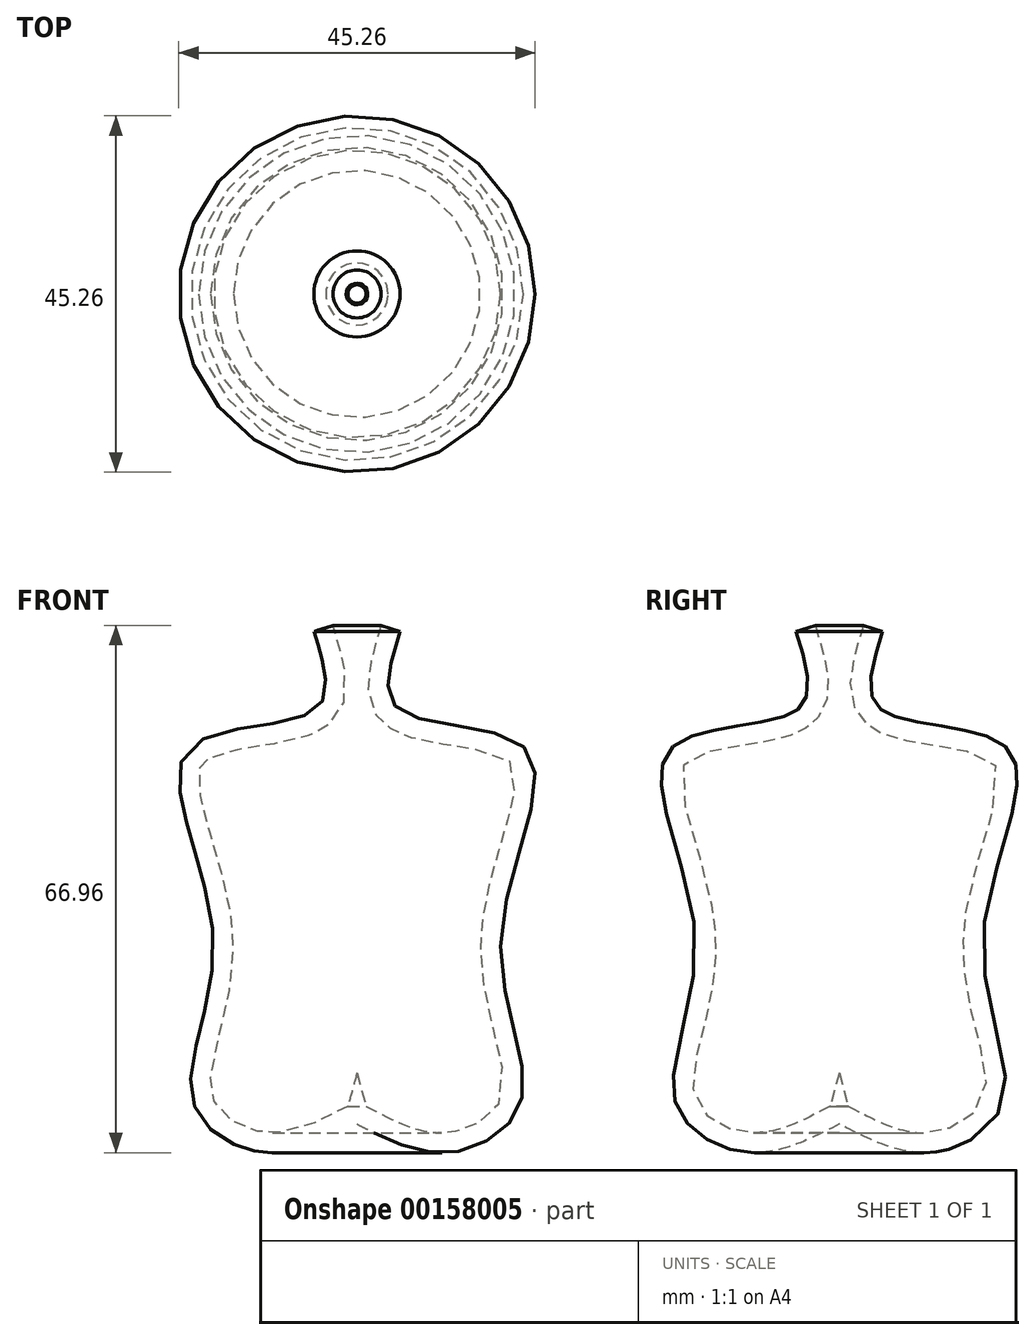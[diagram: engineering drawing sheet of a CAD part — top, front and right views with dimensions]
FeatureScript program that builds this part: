
annotation { "Feature Type Name" : "Feature", "Feature Type Description" : "" }
export const myFeature = defineFeature(function(context is Context, id is Id, definition is map)
    precondition{}
    {
        {
            var Q0;
            Q0=qCreatedBy(makeId("Front.planeOp"),FACE);
            var sketch = newSketch(context, id + "F0", { "sketchPlane" : qUnion([Q0])});
            skFitSpline(sketch, "E0", {"points": [v(0, 0) * mm, v(11.8, -3.6) * mm, v(20.86, 2.9) * mm, v(18.3, 23.93) * mm, v(21.54, 47.53) * mm, v(5.3, 52.66) * mm, v(4.44, 58.98) * mm, v(5.47, 62.57) * mm], "startDerivative": vector(81.88, -42.1) * mm, "endDerivative": vector(12.45, 40.09) * mm});
            skFitSpline(sketch, "E1.0", {"points": [v(1.16, 2.26) * mm, v(2.01, 1.82) * mm, v(3.68, 0.96) * mm, v(6.08, -0.12) * mm, v(7.98, -0.73) * mm, v(9.44, -1.01) * mm, v(10.32, -1.1) * mm, v(11.03, -1.1) * mm, v(11.55, -1.07) * mm, v(12.08, -1) * mm, v(12.8, -0.88) * mm, v(13.7, -0.63) * mm, v(14.75, -0.22) * mm, v(15.72, 0.31) * mm, v(16.59, 0.93) * mm, v(17.31, 1.62) * mm, v(17.88, 2.36) * mm, v(18.21, 2.99) * mm, v(18.4, 3.5) * mm, v(18.53, 4.05) * mm, v(18.61, 4.85) * mm, v(18.57, 6.02) * mm, v(18.38, 7.39) * mm, v(17.97, 9.43) * mm, v(17.22, 12.33) * mm, v(16.44, 15.64) * mm, v(15.96, 18.5) * mm, v(15.73, 20.74) * mm, v(15.69, 22.7) * mm, v(15.76, 24.3) * mm, v(15.92, 25.9) * mm, v(16.23, 27.9) * mm, v(16.75, 30.25) * mm, v(17.36, 32.55) * mm, v(18, 34.77) * mm, v(18.64, 36.9) * mm, v(19.2, 38.9) * mm, v(19.68, 40.74) * mm, v(20, 42.39) * mm, v(20.12, 43.78) * mm, v(20.07, 44.67) * mm, v(19.96, 45.19) * mm, v(19.86, 45.49) * mm, v(19.76, 45.68) * mm, v(19.67, 45.8) * mm, v(19.6, 45.9) * mm, v(19.5, 45.99) * mm, v(19.36, 46.12) * mm, v(19.1, 46.31) * mm, v(18.69, 46.55) * mm, v(18, 46.86) * mm, v(16.9, 47.22) * mm, v(15.3, 47.59) * mm, v(13.55, 47.9) * mm, v(11.7, 48.18) * mm, v(9.84, 48.48) * mm, v(8.01, 48.84) * mm, v(6.55, 49.23) * mm, v(5.42, 49.66) * mm, v(4.74, 50) * mm, v(4.2, 50.32) * mm, v(3.8, 50.6) * mm, v(3.43, 50.9) * mm, v(2.96, 51.35) * mm, v(2.47, 51.97) * mm, v(1.87, 53.03) * mm, v(1.47, 54.39) * mm, v(1.37, 55.9) * mm, v(1.49, 57.29) * mm, v(1.68, 58.32) * mm, v(1.85, 59.07) * mm, v(1.97, 59.57) * mm, v(2.1, 60.04) * mm, v(2.25, 60.62) * mm, v(2.43, 61.3) * mm, v(2.72, 62.26) * mm, v(2.92, 62.9) * mm, v(3.05, 63.33) * mm]});
            skLineSegment(sketch, "E2", {"start": v(5.47, 62.57) * mm, "end": v(3.05, 63.33) * mm});
            skLineSegment(sketch, "E3", {"start": v(0, 0) * mm, "end": v(1.16, 2.26) * mm});
            skLineSegment(sketch, "E4", {"start": v(0, 0) * mm, "end": v(0, 6.5) * mm});
            skLineSegment(sketch, "E5", {"start": v(1.16, 2.26) * mm, "end": v(0, 6.5) * mm});
            skSolve(sketch);
        }
        {
            var Q0;
            Q0=makeQuery(id+"F0.imprint","IMPRINT",FACE,{"disambiguationData":[TD([[makeQuery(id+"F0.imprint","IMPRINT",EDGE,{"derivedFrom":sQuery(id+"F0.wireOp",EDGE,"E0")}),1.0]])]});
            var Q1;
            Q1=makeQuery(id+"F0.imprint","IMPRINT",FACE,{"disambiguationData":[TD([[makeQuery(id+"F0.imprint","IMPRINT",EDGE,{"derivedFrom":sQuery(id+"F0.wireOp",EDGE,"E3")}),1.0]])]});
            var Q2;
            Q2=sQuery(id+"F0.wireOp",EDGE,"E4");
            revolve(context, id + "F1", {"entities" : qUnion([Q0, Q1]), "axis" : qUnion([Q2]), "revolveType" : RevolveType.FULL});
        }
        {
            var Q0;
            Q0=qCreatedBy(makeId("Front.planeOp"),FACE);
            var sketch = newSketch(context, id + "F2", { "sketchPlane" : qUnion([Q0])});
            skFitSpline(sketch, "E6", {"points": [v(22.05, 42.91) * mm, v(30.26, 44.96) * mm, v(34.53, 35.9) * mm, v(20.17, 11.97) * mm], "startDerivative": vector(34.07, 17.32) * mm, "endDerivative": vector(-44.63, -54.2) * mm});
            skFitSpline(sketch, "E7.0", {"points": [v(22.49, 42.06) * mm, v(23.2, 42.42) * mm, v(24.6, 43.13) * mm, v(26.25, 43.83) * mm, v(27.47, 44.17) * mm, v(28.32, 44.3) * mm, v(29.1, 44.29) * mm, v(29.68, 44.17) * mm, v(30.13, 44) * mm, v(30.57, 43.76) * mm, v(31.12, 43.35) * mm, v(31.75, 42.7) * mm, v(32.5, 41.6) * mm, v(33.26, 39.9) * mm, v(33.62, 37.86) * mm, v(33.62, 36.13) * mm, v(33.4, 34.34) * mm, v(32.75, 31.98) * mm, v(31.41, 28.98) * mm, v(28.99, 24.8) * mm, v(25, 19.34) * mm, v(21.3, 14.83) * mm, v(19.44, 12.57) * mm]});
            skLineSegment(sketch, "E8", {"start": v(22.49, 42.06) * mm, "end": v(22.05, 42.91) * mm});
            skLineSegment(sketch, "E9", {"start": v(19.44, 12.57) * mm, "end": v(20.17, 11.97) * mm});
            skSolve(sketch);
        }
        {
            var Q0;
            Q0=makeQuery(id+"F2.imprint","IMPRINT",FACE,{"disambiguationData":[TD([[makeQuery(id+"F2.imprint","IMPRINT",EDGE,{"derivedFrom":sQuery(id+"F2.wireOp",EDGE,"E6")}),-1.0]])]});
            var Q1;
            Q1=sQuery(id+"F2.wireOp",EDGE,"E6");
            var Q2;
            Q2=makeQuery(id+"F1.opRevolve","SWEPT_FACE",FACE,{"disambiguationData":[OSD([sQuery(id+"F0.wireOp",EDGE,"E0")])]});
            revolve(context, id + "F3", {"bodyType" : ToolBodyType.SURFACE, "operationType" : NewBodyOperationType.INTERSECT, "entities" : qUnion([Q0]), "surfaceEntities" : qUnion([Q1]), "axis" : qUnion([Q2]), "revolveType" : RevolveType.ONE_DIRECTION, "angle" : 10 * degree});
        }
    });
